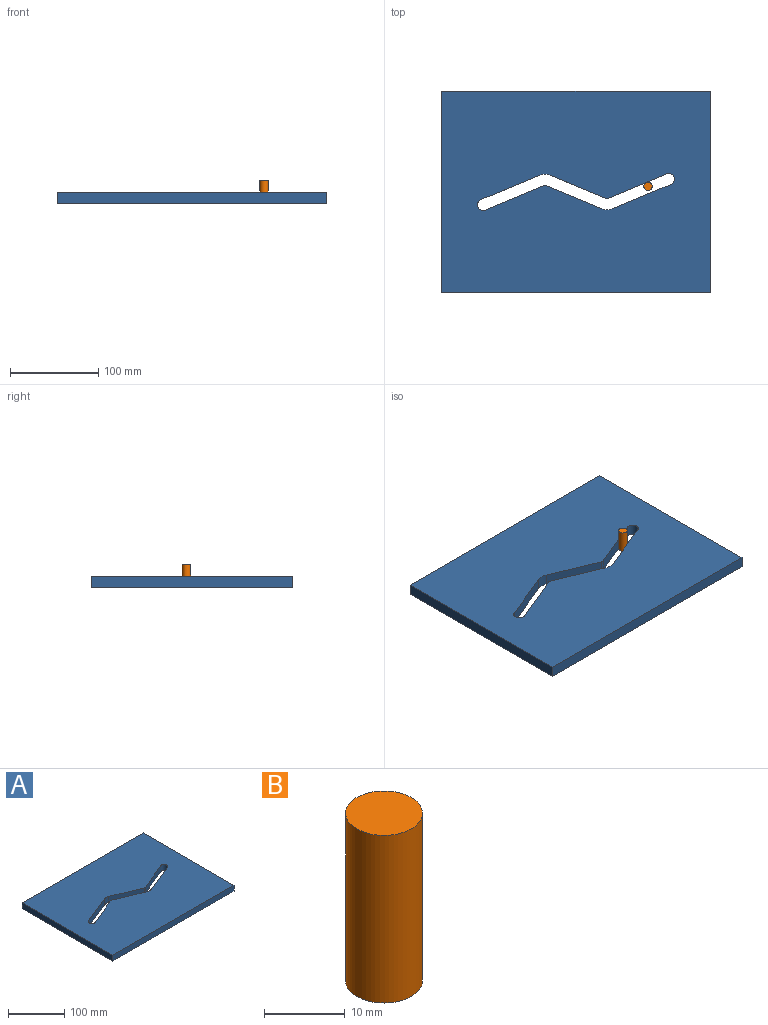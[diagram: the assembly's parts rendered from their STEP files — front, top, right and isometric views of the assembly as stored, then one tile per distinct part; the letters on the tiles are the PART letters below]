
ASSEMBLY  parts=2 mates=1
PART A: 18 faces, bbox 304.8x228.6x12.7 mm
  f0: cylinder r=6.38mm len=12.7mm, axis (0,0,-1), area 254.4mm2, adj f1,f11,f12,f13
  f1: plane 66.76x27.65mm, normal (0.38,-0.92,0), area 917.8mm2, adj f0,f12,f13,f14
  f2: plane 63.11x26.14mm, normal (-0.38,-0.92,0), area 867.5mm2, adj f12,f13,f14,f16
  f3: plane 66.75x27.65mm, normal (0.38,-0.92,0), area 917.5mm2, adj f4,f12,f13,f16
  f4: cylinder r=6.38mm len=12.7mm, axis (0,0,-1), area 254.4mm2, adj f3,f5,f12,f13
  f5: plane 66.76x27.65mm, normal (-0.38,0.92,0), area 917.8mm2, adj f4,f12,f13,f15
  f6: plane 63.11x26.14mm, normal (0.38,0.92,0), area 867.5mm2, adj f12,f13,f15,f17
  f7: plane 228.6x12.7mm, normal (1,0,0), area 2903.2mm2, adj f8,f10,f12,f13
  f8: plane 304.8x12.7mm, normal (0,1,0), area 3871mm2, adj f7,f9,f12,f13
  f9: plane 228.6x12.7mm, normal (-1,0,0), area 2903.2mm2, adj f8,f10,f12,f13
  f10: plane 304.8x12.7mm, normal (0,-1,0), area 3871mm2, adj f7,f9,f12,f13
  f11: plane 66.75x27.65mm, normal (-0.38,0.92,0), area 917.5mm2, adj f0,f12,f13,f17
  f12: plane 304.8x228.6mm, normal (0,0,1), area 66645.2mm2, adj f0,f1,f2,f3,f4,f5,f6,f7
  f13: plane 304.8x228.6mm, normal (0,0,-1), area 66645.2mm2, adj f0,f1,f2,f3,f4,f5,f6,f7
  f14: cylinder r=15.88mm len=12.7mm, axis (0,0,1), area 158.3mm2, adj f1,f2,f12,f13
  f15: cylinder r=15.88mm len=12.7mm, axis (0,0,1), area 158.3mm2, adj f5,f6,f12,f13
  f16: cylinder r=3.17mm len=12.7mm, axis (0,0,-1), area 31.7mm2, adj f2,f3,f12,f13
  f17: cylinder r=3.17mm len=12.7mm, axis (0,0,-1), area 31.7mm2, adj f6,f11,f12,f13
PART B: 3 faces, bbox 9.5x9.5x25.4 mm
  f0: cylinder r=4.76mm len=25.4mm, axis (0,0,-1), area 760.1mm2, adj f1,f2
  f1: plane 9.53x9.53mm, normal (0,0,1), area 71.3mm2, adj f0
  f2: plane 9.53x9.53mm, normal (0,0,-1), area 71.3mm2, adj f0
PLACE A t=(0,-114.3,-6.35)mm
PLACE B rot(axis=(0,0,-1),85.3deg) t=(-50.77,339.29,-12.7)mm
MATE planar B.f0 <-> A.f13  axis (0,0,-1) through (81.78,120.76,-12.7)mm
